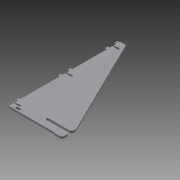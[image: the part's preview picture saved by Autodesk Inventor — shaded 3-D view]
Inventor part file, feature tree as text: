
AUTODESK INVENTOR PART (.ipt)
format: ipt  version: 2015 SP2 (Build 190223200, 223)  size: 220,160 bytes
history: native  units: mm
features: extrude x6, sketch x6, chamfer x2
ambient origin geometry x8: Origin, YZ Plane, XZ Plane, XY Plane, X Axis, Y Axis, Z Axis, Center Point
bodies: Solid1 (feature_tree)
feature tree (14):
  extrude  "Extrusion1"  Depth=183.9mm
  extrude  "Extrusion2"  Depth=47.0mm
  extrude  "Extrusion3"  Depth=9.0mm
  extrude  "Extrusion4"  Depth=9.0mm
  extrude  "Extrusion5"  Depth=6.0mm
  extrude  "Extrusion6"  Depth=6.0mm TaperAngle=0.0deg
  chamfer  "Chamfer1"  Distance=5.1mm
  chamfer  "Chamfer2"  Distance=4.4mm
  sketch  "Sketch1"  dims[d0=370.0mm d1=183.9mm]
  sketch  "Sketch2"  dims[d2=25.4mm d3=47.0mm]
  sketch  "Sketch3"  dims[d4=6.0mm d5=0.0mm d6=9.0mm]
  sketch  "Sketch4"  dims[d7=9.0mm d8=9.0mm]
  sketch  "Sketch5"  dims[d9=9.0mm d12=6.0mm]
  sketch  "Sketch6"  dims[d14=9.0mm d18=6.0mm d19=0.0mm d20=5.1mm d21=4.4mm d22=17.1mm d23=21.1mm d25=8.0mm d28=6.0mm d29=0.0mm d32=6.0mm d33=0.0mm d34=8.8mm d35=2.0mm d36=150.8mm d37=28.0mm d38=75.0mm d39=6.0mm d40=0.0mm d41=8.0mm d42=8.0mm d43=8.0mm d44=24.0mm d45=6.0mm d46=0.0mm d47=2.0mm d48=2.0mm d49=45.0deg d50=5.0mm d51=2.0mm d52=45.0deg d53=32.15mm d54=171.35mm d55=203.65mm d56=326.443mm d57=358.743mm d58=192.0mm d59=20.51mm d60=347.093mm]
